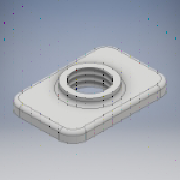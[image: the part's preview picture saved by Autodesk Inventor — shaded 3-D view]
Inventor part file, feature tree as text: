
AUTODESK INVENTOR PART (.ipt)
format: ipt  version: 2018 (Build 220112000, 112)  size: 177,664 bytes
history: native  units: mm
features: extrude x2, fillet x2, sketch x2, thread x1
ambient origin geometry x8: Origin, YZ Plane, XZ Plane, XY Plane, X Axis, Y Axis, Z Axis, Center Point
bodies: Solid1 (feature_tree)
feature tree (7):
  extrude  "Extrusion1"  Depth=15.0mm
  extrude  "Extrusion2"  Depth=2.0mm
  fillet  "Fillet1"  Radius=1.5mm
  thread  "Thread1"  [1 undecoded]
  fillet  "Fillet2"  Radius=1.0mm
  sketch  "Sketch1"  dims[d0=10.0mm d1=15.0mm]
  sketch  "Sketch2"  dims[d2=4.8mm d3=2.0mm d4=1.5mm d5=0.0mm d6=6.5mm d7=1.0mm d8=0.0mm d9=0.5mm d10=10.0mm d11=0.0mm d12=0.5mm]
note: 1 required parameter value undecoded (feature->parameter linkage not recoverable at this tier; creation-order binding heuristic only, values carry confidence <= 0.55)
